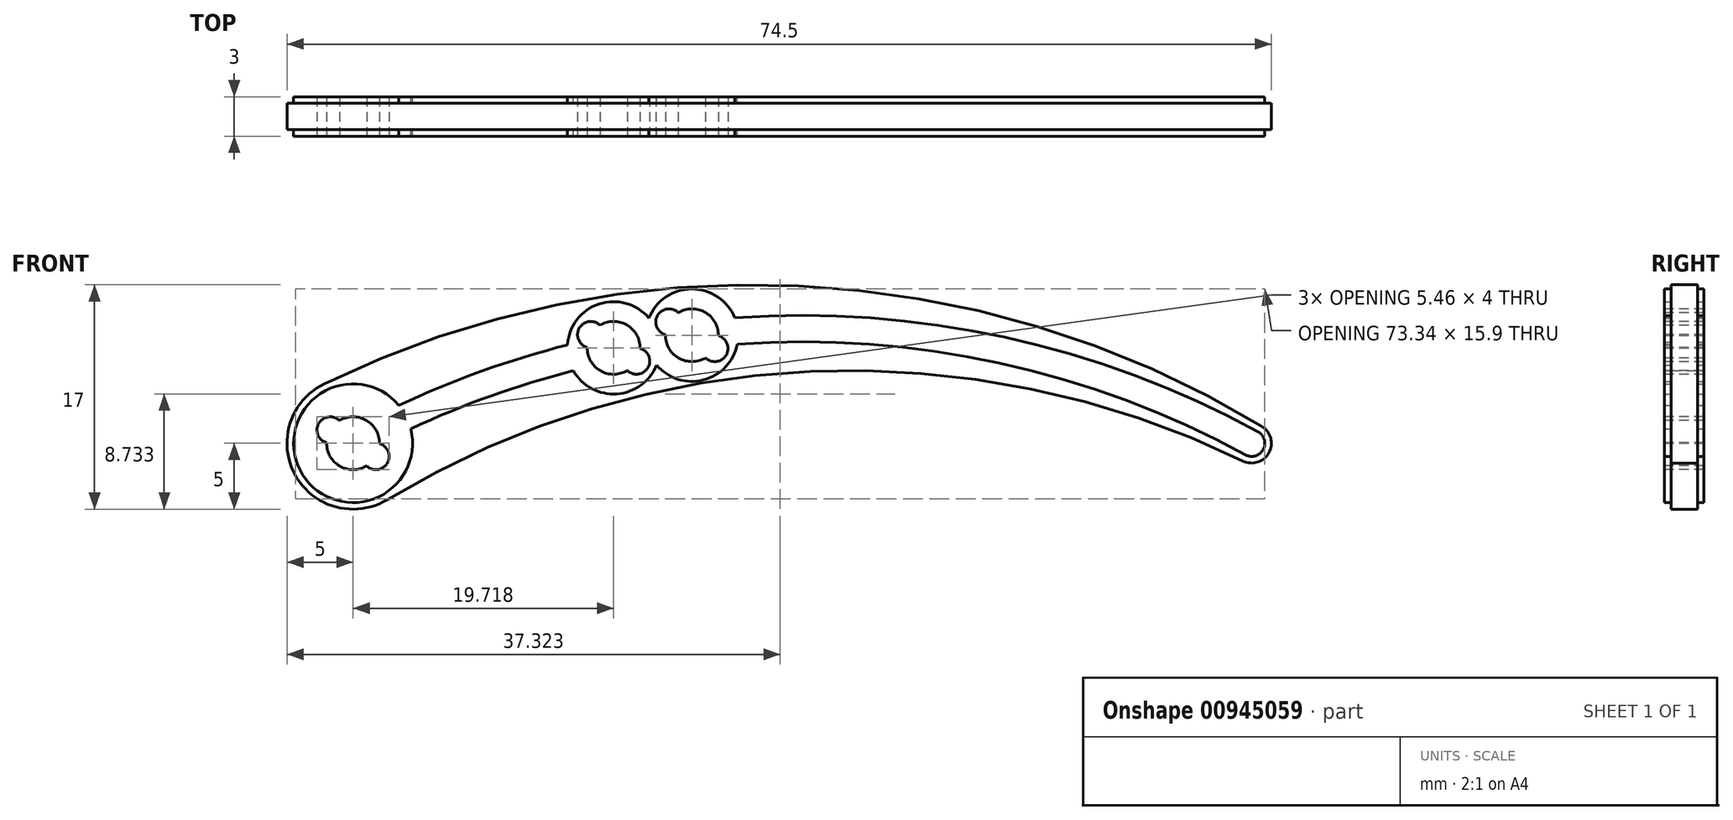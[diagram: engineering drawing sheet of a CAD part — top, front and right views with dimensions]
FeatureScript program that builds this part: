
annotation { "Feature Type Name" : "Feature", "Feature Type Description" : "" }
export const myFeature = defineFeature(function(context is Context, id is Id, definition is map)
    precondition{}
    {
        {
            var Q0;
            Q0=qCreatedBy(makeId("Front.planeOp"),FACE);
            var sketch = newSketch(context, id + "F0", { "sketchPlane" : qUnion([Q0])});
            skArc(sketch, "E0", {"start": v(-2.2, 4.5) * mm, "mid": v(-4.4, -2.4) * mm, "end": v(2.59, -4.28) * mm});
            skArc(sketch, "E1", {"start": v(67.34, -1.35) * mm, "mid": v(69.32, -0.72) * mm, "end": v(68.78, 1.28) * mm});
            skArc(sketch, "E2", {"start": v(68.78, 1.28) * mm, "mid": v(33.7, 11.92) * mm, "end": v(-2.2, 4.5) * mm});
            skArc(sketch, "E3", {"start": v(67.34, -1.35) * mm, "mid": v(34.6, 5.43) * mm, "end": v(2.59, -4.28) * mm});
            skSolve(sketch);
        }
        {
            var Q0;
            Q0=makeQuery(id+"F0.imprint","IMPRINT",FACE,{"disambiguationData":[TD([[makeQuery(id+"F0.imprint","IMPRINT",EDGE,{"derivedFrom":sQuery(id+"F0.wireOp",EDGE,"E0")}),1.0]])]});
            extrude(context, id + "F1", {"entities" : qUnion([Q0]), "depth" : 2 * mm, "offsetDistance" : 25 * mm, "symmetric" : true});
        }
        {
            var Q0;
            Q0=qCreatedBy(makeId("Front.planeOp"),FACE);
            var sketch = newSketch(context, id + "F2", { "sketchPlane" : qUnion([Q0])});
            skArc(sketch, "E4", {"start": v(3.46, 2.87) * mm, "mid": v(-4.01, -2.03) * mm, "end": v(4.37, 1.09) * mm});
            skArc(sketch, "E5", {"start": v(67.52, -0.88) * mm, "mid": v(68.88, -0.48) * mm, "end": v(68.48, 0.88) * mm});
            skArc(sketch, "E6", {"start": v(68.48, 0.88) * mm, "mid": v(49.3, 8.03) * mm, "end": v(28.89, 9.5) * mm});
            skArc(sketch, "E7", {"start": v(67.52, -0.88) * mm, "mid": v(48.9, 6.07) * mm, "end": v(29.07, 7.5) * mm});
            skArc(sketch, "E8", {"start": v(68, 0) * mm, "mid": v(34, 8.68) * mm, "end": v(0, 0) * mm, "construction": true});
            skPoint(sketch, "E9", {"position": v(37.66, -62.27) * mm});
            skArc(sketch, "E10", {"start": v(22.4, 9.48) * mm, "mid": v(18.62, 10.55) * mm, "end": v(16.23, 7.45) * mm});
            skArc(sketch, "E11", {"start": v(22.97, 5.92) * mm, "mid": v(26.52, 4.8) * mm, "end": v(29.07, 7.5) * mm});
            skArc(sketch, "E12.trimOffspring", {"start": v(16.23, 7.45) * mm, "mid": v(9.74, 5.46) * mm, "end": v(3.46, 2.87) * mm});
            skArc(sketch, "E13.trimOffspring", {"start": v(16.67, 5.5) * mm, "mid": v(10.42, 3.58) * mm, "end": v(4.37, 1.09) * mm});
            skArc(sketch, "E14.trimOffspring", {"start": v(28.89, 9.5) * mm, "mid": v(25.63, 11.68) * mm, "end": v(22.4, 9.48) * mm});
            skArc(sketch, "E15.trimOffspring", {"start": v(16.67, 5.5) * mm, "mid": v(19.95, 3.73) * mm, "end": v(22.97, 5.92) * mm});
            skSolve(sketch);
        }
        {
            var Q0;
            Q0=makeQuery(id+"F2.imprint","IMPRINT",FACE,{"disambiguationData":[TD([[makeQuery(id+"F2.imprint","IMPRINT",EDGE,{"derivedFrom":sQuery(id+"F2.wireOp",EDGE,"E4")}),1.0]])]});
            extrude(context, id + "F3", {"entities" : qUnion([Q0]), "operationType" : NewBodyOperationType.ADD, "depth" : 3 * mm, "offsetDistance" : 25 * mm, "symmetric" : true});
        }
        {
            var Q0;
            Q0=makeQuery(id+"F3.opExtrude","CAP_FACE",FACE,{"disambiguationData":[OSD([sQuery(id+"F2.wireOp",EDGE,"E4"),sQuery(id+"F2.wireOp",EDGE,"E5"),sQuery(id+"F2.wireOp",EDGE,"E6"),sQuery(id+"F2.wireOp",EDGE,"E7"),sQuery(id+"F2.wireOp",EDGE,"E10"),sQuery(id+"F2.wireOp",EDGE,"E11"),sQuery(id+"F2.wireOp",EDGE,"E12.trimOffspring"),sQuery(id+"F2.wireOp",EDGE,"E13.trimOffspring"),sQuery(id+"F2.wireOp",EDGE,"E14.trimOffspring"),sQuery(id+"F2.wireOp",EDGE,"E15.trimOffspring")])],"isStart":false});
            var sketch = newSketch(context, id + "F4", { "sketchPlane" : qUnion([Q0])});
            skArc(sketch, "E16", {"start": v(2, -0.04) * mm, "mid": v(1, 1.73) * mm, "end": v(-1.03, 1.71) * mm});
            skArc(sketch, "E17", {"start": v(-1.03, 1.71) * mm, "mid": v(-2.6, 1.5) * mm, "end": v(-2, 0.04) * mm});
            skArc(sketch, "E18", {"start": v(1.03, -1.71) * mm, "mid": v(2.6, -1.5) * mm, "end": v(2, -0.04) * mm});
            skLineSegment(sketch, "E19", {"start": v(-1.73, 1) * mm, "end": v(1.73, -1) * mm, "construction": true});
            skArc(sketch, "E20.trimOffspring", {"start": v(-2, 0.04) * mm, "mid": v(-1, -1.73) * mm, "end": v(1.03, -1.71) * mm});
            skArc(sketch, "E21", {"start": v(21.72, 7.19) * mm, "mid": v(20.72, 8.96) * mm, "end": v(18.69, 8.94) * mm});
            skArc(sketch, "E22", {"start": v(18.69, 8.94) * mm, "mid": v(17.12, 8.73) * mm, "end": v(17.72, 7.26) * mm});
            skArc(sketch, "E23", {"start": v(20.75, 5.51) * mm, "mid": v(22.32, 5.73) * mm, "end": v(21.72, 7.19) * mm});
            skLineSegment(sketch, "E24", {"start": v(17.99, 8.23) * mm, "end": v(21.45, 6.23) * mm, "construction": true});
            skArc(sketch, "E25.trimOffspring", {"start": v(17.72, 7.26) * mm, "mid": v(18.72, 5.5) * mm, "end": v(20.75, 5.51) * mm});
            skArc(sketch, "E26", {"start": v(27.64, 8.15) * mm, "mid": v(26.64, 9.92) * mm, "end": v(24.6, 9.9) * mm});
            skArc(sketch, "E27", {"start": v(24.6, 9.9) * mm, "mid": v(23.04, 9.68) * mm, "end": v(23.64, 8.22) * mm});
            skArc(sketch, "E28", {"start": v(26.67, 6.47) * mm, "mid": v(28.24, 6.68) * mm, "end": v(27.64, 8.15) * mm});
            skLineSegment(sketch, "E29", {"start": v(23.9, 9.18) * mm, "end": v(27.37, 7.18) * mm, "construction": true});
            skArc(sketch, "E30.trimOffspring", {"start": v(23.64, 8.22) * mm, "mid": v(24.64, 6.45) * mm, "end": v(26.67, 6.47) * mm});
            skSolve(sketch);
        }
        {
            var Q0;
            Q0=makeQuery(id+"F4.imprint","IMPRINT",FACE,{"disambiguationData":[TD([[makeQuery(id+"F4.imprint","IMPRINT",EDGE,{"derivedFrom":sQuery(id+"F4.wireOp",EDGE,"E16")}),1.0]])]});
            var Q1;
            Q1=makeQuery(id+"F4.imprint","IMPRINT",FACE,{"disambiguationData":[TD([[makeQuery(id+"F4.imprint","IMPRINT",EDGE,{"derivedFrom":sQuery(id+"F4.wireOp",EDGE,"E21")}),1.0]])]});
            var Q2;
            Q2=makeQuery(id+"F4.imprint","IMPRINT",FACE,{"disambiguationData":[TD([[makeQuery(id+"F4.imprint","IMPRINT",EDGE,{"derivedFrom":sQuery(id+"F4.wireOp",EDGE,"E26")}),1.0]])]});
            extrude(context, id + "F5", {"entities" : qUnion([Q0, Q1, Q2]), "operationType" : NewBodyOperationType.REMOVE, "endBound" : BoundingType.THROUGH_ALL, "oppositeDirection" : true, "depth" : 25 * mm, "offsetDistance" : 25 * mm});
        }
    });
